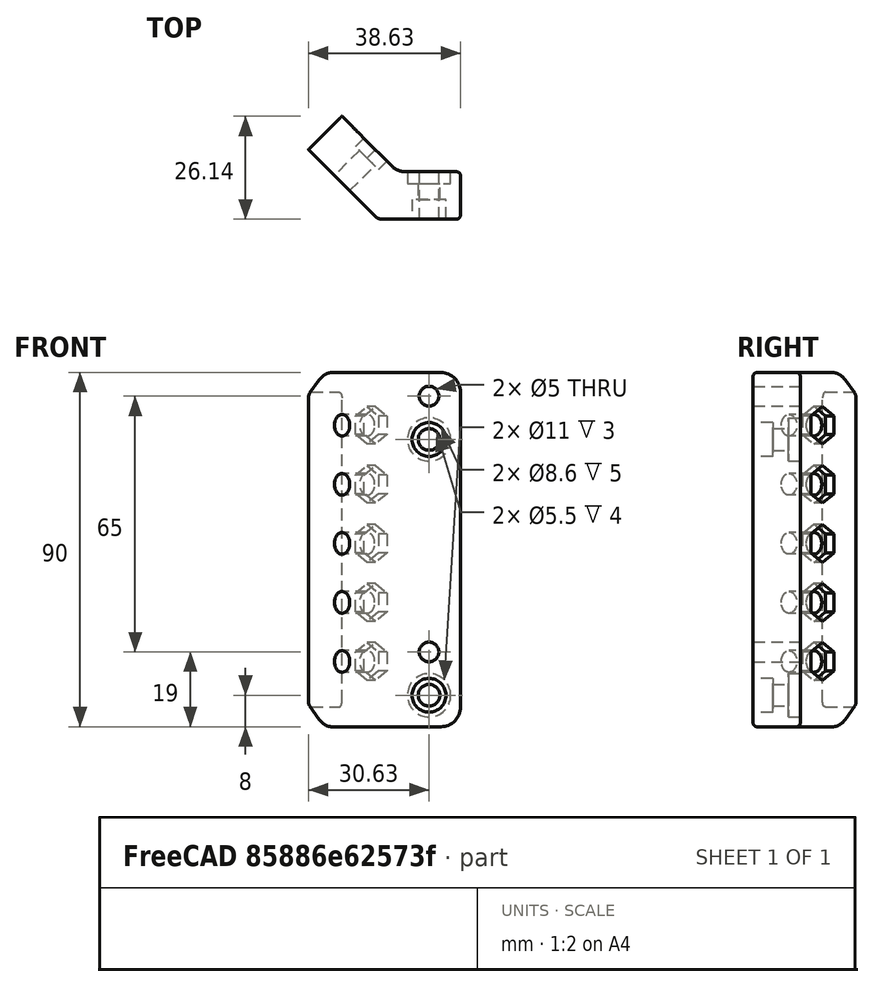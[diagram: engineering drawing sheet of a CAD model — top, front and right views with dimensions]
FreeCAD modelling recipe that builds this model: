
FCSTD DOCUMENT  (FreeCAD 0.19R)
Label: CargiFork
License: All rights reserved
LicenseURL: http://en.wikipedia.org/wiki/All_rights_reserved
objects: Sketcher::SketchObject×7, PartDesign::Pocket×6, PartDesign::Fillet×6, PartDesign::Pad×1, PartDesign::Chamfer×1, PartDesign::Body×1, Mesh::Feature×1
note: 36 computed .brp shape members not serialized (recipe doc carries the construction recipe); baked Part::Feature solids carry a one-line shape summary decoded from their .brp

FEATURE [Sketcher::SketchObject] Sketch
  FullyConstrained = true
  MapMode = 5
  Support = -> [XY_Plane]
  sketch-geometry (6):
    g0: LineSegment StartX=-16 StartY=0 StartZ=0 EndX=0 EndY=0 EndZ=0
    g1: LineSegment StartX=0 StartY=0 StartZ=0 EndX=0 EndY=-12 EndZ=0
    g2: LineSegment StartX=0 StartY=-12 StartZ=0 EndX=-20.9706 EndY=-12 EndZ=0
    g3: LineSegment StartX=-20.9706 StartY=-12 StartZ=0 EndX=-38.6274 EndY=5.65685 EndZ=0
    g4: LineSegment StartX=-38.6274 StartY=5.65685 StartZ=0 EndX=-30.1421 EndY=14.1421 EndZ=0
    g5: LineSegment StartX=-30.1421 StartY=14.1421 StartZ=0 EndX=-16 EndY=0 EndZ=0
  constraints (17):
    c: PointOnObject(g0,g-1)
    c: Coincident(g0,g-1)
    c: Coincident(g0,g1)
    c: PointOnObject(g1,g-2)
    c: Coincident(g1,g2)
    c: Horizontal(g2)
    c: Coincident(g2,g3)
    c: Coincident(g3,g4)
    c: Coincident(g4,g5)
    c: Coincident(g5,g0)
    c: Distance(g1) = 12
    c: Distance(g4) = 12
    c: Perpendicular(g3,g4)
    c: Angle(g5) = -0.785398
    c: Parallel(g3,g5)
    c: Distance(g0) = 16
    c: Distance(g5) = 20
FEATURE [PartDesign::Pad] Pad
  Direction = (1,1,1)
  Length = 90
  Length2 = 100
  Profile = -> Sketch
  Type = 0
FEATURE [Sketcher::SketchObject] Sketch001
  FullyConstrained = true
  MapMode = 5
  Placement = pos=(0,0,0) rot=(0,0.707107,0.707107;3.14159rad)
  Support = -> [Pad]
  sketch-geometry (2):
    g0: Circle CenterX=8 CenterY=73 CenterZ=0 NormalX=0 NormalY=0 NormalZ=1 AngleXU=0 Radius=2.75
    g1: Circle CenterX=8 CenterY=8 CenterZ=0 NormalX=0 NormalY=0 NormalZ=1 AngleXU=0 Radius=2.75
  constraints (6):
    c: Radius(g1) = 2.75
    c: Equal(g1,g0)
    c: DistanceY(g1) = 8
    c: Distance(g1,g0) = 65
    c: DistanceX(g-1,g0) = 8
    c: DistanceX(g1) = 8
FEATURE [PartDesign::Pocket] Pocket
  BaseFeature = -> Pad
  Length = 5
  Length2 = 100
  Profile = -> Sketch001
  Type = 1
FEATURE [Sketcher::SketchObject] Sketch002
  ExternalGeometry = -> [Pocket]
  FullyConstrained = true
  MapMode = 5
  Placement = pos=(0,0,0) rot=(0,0.707107,0.707107;3.14159rad)
  Support = -> [Pocket]
  sketch-geometry (2):
    g0: Circle CenterX=8 CenterY=73 CenterZ=0 NormalX=0 NormalY=0 NormalZ=1 AngleXU=0 Radius=5.5
    g1: Circle CenterX=8 CenterY=8 CenterZ=0 NormalX=0 NormalY=0 NormalZ=1 AngleXU=0 Radius=5.5
  constraints (4):
    c: Radius(g1) = 5.5
    c: Equal(g1,g0)
    c: Coincident(g1,g-4)
    c: Coincident(g0,g-3)
FEATURE [PartDesign::Pocket] Pocket001
  BaseFeature = -> Pocket
  Length = 3
  Length2 = 100
  Profile = -> Sketch002
  Type = 0
FEATURE [Sketcher::SketchObject] Sketch003
  ExternalGeometry = -> [Pocket001]
  FullyConstrained = true
  MapMode = 5
  Placement = pos=(0,-12,0) rot=(1,0,0;1.5708rad)
  Support = -> [Pocket001]
  sketch-geometry (2):
    g0: Circle CenterX=-8 CenterY=73 CenterZ=0 NormalX=0 NormalY=0 NormalZ=1 AngleXU=0 Radius=4.3
    g1: Circle CenterX=-8 CenterY=8 CenterZ=0 NormalX=0 NormalY=0 NormalZ=1 AngleXU=0 Radius=4.3
  constraints (4):
    c: Radius(g1) = 4.3
    c: Equal(g1,g0)
    c: Coincident(g1,g-4)
    c: Coincident(g0,g-3)
FEATURE [PartDesign::Pocket] Pocket002
  BaseFeature = -> Pocket001
  Length = 5
  Length2 = 100
  Profile = -> Sketch003
  Type = 0
FEATURE [Sketcher::SketchObject] Sketch004
  FullyConstrained = false
  MapMode = 5
  Placement = pos=(-16.4853,-16.4853,0) rot=(0.862856,-0.357407,-0.357407;1.71777rad)
  Support = -> [Pocket002]
  sketch-geometry (6):
    g0: Circle CenterX=-19.2578 CenterY=76.595 CenterZ=0 NormalX=0 NormalY=0 NormalZ=1 AngleXU=0 Radius=2.75
    g1: Circle CenterX=-19.2578 CenterY=61.595 CenterZ=0 NormalX=0 NormalY=0 NormalZ=1 AngleXU=0 Radius=2.75
    g2: Circle CenterX=-19.2578 CenterY=46.595 CenterZ=0 NormalX=0 NormalY=0 NormalZ=1 AngleXU=0 Radius=2.75
    g3: Circle CenterX=-19.2578 CenterY=31.595 CenterZ=0 NormalX=0 NormalY=0 NormalZ=1 AngleXU=0 Radius=2.75
    g4: Circle CenterX=-19.2578 CenterY=16.595 CenterZ=0 NormalX=0 NormalY=0 NormalZ=1 AngleXU=0 Radius=2.75
    g5: LineSegment StartX=-19.2578 StartY=117.649 StartZ=0 EndX=-19.2578 EndY=-34.6142 EndZ=0
  constraints (15):
    c: Radius(g0) = 2.75
    c: Equal(g0,g1)
    c: Equal(g0,g2)
    c: Equal(g0,g3)
    c: Vertical(g5)
    c: PointOnObject(g1,g5)
    c: PointOnObject(g0,g5)
    c: PointOnObject(g2,g5)
    c: PointOnObject(g3,g5)
    c: PointOnObject(g4,g5)
    c: Distance(g0,g1) = 15
    c: Distance(g2,g1) = 15
    c: Distance(g3,g2) = 15
    c: Distance(g4,g3) = 15
    c: Radius(g4) = 2.75
FEATURE [PartDesign::Pocket] Pocket003
  BaseFeature = -> Pocket002
  Length = 5
  Length2 = 100
  Profile = -> Sketch004
  Type = 1
FEATURE [Sketcher::SketchObject] Sketch005
  ExternalGeometry = -> [Pocket003]
  FullyConstrained = true
  MapMode = 5
  Placement = pos=(-8,-8,0) rot=(0.281085,0.678598,0.678598;2.59356rad)
  Support = -> [Pocket003]
  sketch-geometry (35):
    g0: LineSegment StartX=19.2578 StartY=71.803 StartZ=0 EndX=23.4078 EndY=74.199 EndZ=0
    g1: LineSegment StartX=23.4078 StartY=74.199 StartZ=0 EndX=23.4078 EndY=78.991 EndZ=0
    g2: LineSegment StartX=23.4078 StartY=78.991 StartZ=0 EndX=19.2578 EndY=81.387 EndZ=0
    g3: LineSegment StartX=19.2578 StartY=81.387 StartZ=0 EndX=15.1078 EndY=78.991 EndZ=0
    g4: LineSegment StartX=15.1078 StartY=78.991 StartZ=0 EndX=15.1078 EndY=74.199 EndZ=0
    g5: LineSegment StartX=15.1078 StartY=74.199 StartZ=0 EndX=19.2578 EndY=71.803 EndZ=0
    g6: Circle CenterX=19.2578 CenterY=76.595 CenterZ=0 NormalX=0 NormalY=0 NormalZ=1 AngleXU=0 Radius=4.79201
    g7: LineSegment StartX=23.4078 StartY=59.199 StartZ=0 EndX=23.4078 EndY=63.991 EndZ=0
    g8: LineSegment StartX=23.4078 StartY=63.991 StartZ=0 EndX=19.2578 EndY=66.387 EndZ=0
    g9: LineSegment StartX=19.2578 StartY=66.387 StartZ=0 EndX=15.1078 EndY=63.991 EndZ=0
    g10: LineSegment StartX=15.1078 StartY=63.991 StartZ=0 EndX=15.1078 EndY=59.199 EndZ=0
    g11: LineSegment StartX=15.1078 StartY=59.199 StartZ=0 EndX=19.2578 EndY=56.803 EndZ=0
    g12: LineSegment StartX=19.2578 StartY=56.803 StartZ=0 EndX=23.4078 EndY=59.199 EndZ=0
    g13: Circle CenterX=19.2578 CenterY=61.595 CenterZ=0 NormalX=0 NormalY=0 NormalZ=1 AngleXU=0 Radius=4.79201
    g14: LineSegment StartX=19.2578 StartY=41.803 StartZ=0 EndX=23.4078 EndY=44.199 EndZ=0
    g15: LineSegment StartX=23.4078 StartY=44.199 StartZ=0 EndX=23.4078 EndY=48.991 EndZ=0
    g16: LineSegment StartX=23.4078 StartY=48.991 StartZ=0 EndX=19.2578 EndY=51.387 EndZ=0
    g17: LineSegment StartX=19.2578 StartY=51.387 StartZ=0 EndX=15.1078 EndY=48.991 EndZ=0
    g18: LineSegment StartX=15.1078 StartY=48.991 StartZ=0 EndX=15.1078 EndY=44.199 EndZ=0
    g19: LineSegment StartX=15.1078 StartY=44.199 StartZ=0 EndX=19.2578 EndY=41.803 EndZ=0
    g20: Circle CenterX=19.2578 CenterY=46.595 CenterZ=0 NormalX=0 NormalY=0 NormalZ=1 AngleXU=0 Radius=4.79201
    g21: LineSegment StartX=19.2578 StartY=26.803 StartZ=0 EndX=23.4078 EndY=29.199 EndZ=0
    g22: LineSegment StartX=23.4078 StartY=29.199 StartZ=0 EndX=23.4078 EndY=33.991 EndZ=0
    g23: LineSegment StartX=23.4078 StartY=33.991 StartZ=0 EndX=19.2578 EndY=36.387 EndZ=0
    g24: LineSegment StartX=19.2578 StartY=36.387 StartZ=0 EndX=15.1078 EndY=33.991 EndZ=0
    g25: LineSegment StartX=15.1078 StartY=33.991 StartZ=0 EndX=15.1078 EndY=29.199 EndZ=0
    g26: LineSegment StartX=15.1078 StartY=29.199 StartZ=0 EndX=19.2578 EndY=26.803 EndZ=0
    g27: Circle CenterX=19.2578 CenterY=31.595 CenterZ=0 NormalX=0 NormalY=0 NormalZ=1 AngleXU=0 Radius=4.79201
    g28: LineSegment StartX=19.2578 StartY=11.803 StartZ=0 EndX=23.4078 EndY=14.199 EndZ=0
    g29: LineSegment StartX=23.4078 StartY=14.199 StartZ=0 EndX=23.4078 EndY=18.991 EndZ=0
    g30: LineSegment StartX=23.4078 StartY=18.991 StartZ=0 EndX=19.2578 EndY=21.387 EndZ=0
    g31: LineSegment StartX=19.2578 StartY=21.387 StartZ=0 EndX=15.1078 EndY=18.991 EndZ=0
    g32: LineSegment StartX=15.1078 StartY=18.991 StartZ=0 EndX=15.1078 EndY=14.199 EndZ=0
    g33: LineSegment StartX=15.1078 StartY=14.199 StartZ=0 EndX=19.2578 EndY=11.803 EndZ=0
    g34: Circle CenterX=19.2578 CenterY=16.595 CenterZ=0 NormalX=0 NormalY=0 NormalZ=1 AngleXU=0 Radius=4.79201
  constraints (80):
    c: Coincident(g0,g1)
    c: Coincident(g1,g2)
    c: Coincident(g2,g3)
    c: Coincident(g3,g4)
    c: Coincident(g4,g5)
    c: Coincident(g5,g0)
    c: Equal(g0, g1-g5) x5
    c: PointOnObject(g0,g6)
    c: PointOnObject(g1,g6)
    c: PointOnObject(g2,g6)
    c: PointOnObject(g3,g6)
    c: PointOnObject(g4,g6)
    c: PointOnObject(g5,g6)
    c: Distance(g0,g1) = 8.3
    c: Coincident(g6,g-3)
    c: Coincident(g7,g8)
    c: Coincident(g8,g9)
    c: Coincident(g9,g10)
    c: Coincident(g10,g11)
    c: Coincident(g11,g12)
    c: Coincident(g12,g7)
    c: Equal(g7, g8-g12) x5
    c: PointOnObject(g7,g13)
    c: PointOnObject(g8,g13)
    c: PointOnObject(g9,g13)
    c: PointOnObject(g10,g13)
    c: PointOnObject(g11,g13)
    c: PointOnObject(g12,g13)
    c: Coincident(g14,g15)
    c: Coincident(g15,g16)
    c: Coincident(g16,g17)
    c: Coincident(g17,g18)
    c: Coincident(g18,g19)
    c: Coincident(g19,g14)
    c: Equal(g14, g15-g19) x5
    c: PointOnObject(g14,g20)
    c: PointOnObject(g15,g20)
    c: PointOnObject(g16,g20)
    c: PointOnObject(g17,g20)
    c: PointOnObject(g18,g20)
    c: PointOnObject(g19,g20)
    c: Coincident(g21,g22)
    c: Coincident(g22,g23)
    c: Coincident(g23,g24)
    c: Coincident(g24,g25)
    c: Coincident(g25,g26)
    c: Coincident(g26,g21)
    c: Equal(g21, g22-g26) x5
    c: PointOnObject(g21,g27)
    c: PointOnObject(g22,g27)
    c: PointOnObject(g23,g27)
    c: PointOnObject(g24,g27)
    c: PointOnObject(g25,g27)
    c: PointOnObject(g26,g27)
    c: Coincident(g28,g29)
    c: Coincident(g29,g30)
    c: Coincident(g30,g31)
    c: Coincident(g31,g32)
    c: Coincident(g32,g33)
    c: Coincident(g33,g28)
    c: Equal(g28, g29-g33) x5
    c: PointOnObject(g28,g34)
    c: PointOnObject(g29,g34)
    c: PointOnObject(g30,g34)
    c: PointOnObject(g31,g34)
    c: PointOnObject(g32,g34)
    c: PointOnObject(g33,g34)
    c: Distance(g28,g30) = 8.3
    c: Distance(g21,g23) = 8.3
    c: Distance(g14,g16) = 8.3
    c: Distance(g7,g8) = 8.3
    c: Coincident(g34,g-7)
    c: Coincident(g27,g-6)
    c: Coincident(g20,g-5)
    c: Coincident(g13,g-4)
    c: Vertical(g1)
    c: Vertical(g7)
    c: Vertical(g15)
    c: Vertical(g22)
    c: Vertical(g29)
FEATURE [PartDesign::Pocket] Pocket004
  BaseFeature = -> Pocket003
  Length = 3
  Length2 = 100
  Profile = -> Sketch005
  Type = 0
FEATURE [Sketcher::SketchObject] Sketch006
  FullyConstrained = true
  MapMode = 5
  Placement = pos=(0,0,0) rot=(0,0.707107,0.707107;3.14159rad)
  Support = -> [Pocket004]
  sketch-geometry (2):
    g0: Circle CenterX=8 CenterY=84 CenterZ=0 NormalX=0 NormalY=0 NormalZ=1 AngleXU=0 Radius=2.5
    g1: Circle CenterX=8 CenterY=19 CenterZ=0 NormalX=0 NormalY=0 NormalZ=1 AngleXU=0 Radius=2.5
  constraints (6):
    c: Radius(g1) = 2.5
    c: Equal(g1,g0)
    c: DistanceX(g0) = 8
    c: DistanceX(g1) = 8
    c: Distance(g0,g1) = 65
    c: DistanceY(g1) = 19
FEATURE [PartDesign::Pocket] Pocket005
  BaseFeature = -> Pocket004
  Length = 5
  Length2 = 100
  Profile = -> Sketch006
  Type = 1
FEATURE [PartDesign::Fillet] Fillet
  Base = -> Pocket005 [Edge46,Edge42]
  BaseFeature = -> Pocket005
  Radius = 5
  SupportTransform = false
FEATURE [PartDesign::Chamfer] Chamfer
  Angle = 45
  Base = -> Fillet [Edge14,Edge54]
  BaseFeature = -> Fillet
  ChamferType = 0
  FlipDirection = false
  Size = 5
  Size2 = 1
  SupportTransform = false
FEATURE [PartDesign::Fillet] Fillet001
  Base = -> Chamfer [Edge2,Edge71]
  BaseFeature = -> Chamfer
  Radius = 6
  SupportTransform = false
FEATURE [PartDesign::Fillet] Fillet002
  Base = -> Fillet001 [Edge54]
  BaseFeature = -> Fillet001
  Radius = 2
  SupportTransform = false
FEATURE [PartDesign::Fillet] Fillet003
  Base = -> Fillet002 [Edge35]
  BaseFeature = -> Fillet002
  Radius = 5
  SupportTransform = false
FEATURE [PartDesign::Fillet] Fillet004
  Base = -> Fillet003 [Edge5]
  BaseFeature = -> Fillet003
  Radius = 1
  SupportTransform = false
FEATURE [PartDesign::Fillet] Fillet005
  Base = -> Fillet004 [Edge3]
  BaseFeature = -> Fillet004
  Radius = 1
  SupportTransform = false
FEATURE [PartDesign::Body] Body
  Group = -> [Sketch,Pad,Sketch001,Pocket,Sketch002,Pocket001,Sketch003,Pocket002,Sketch004,Pocket003,Sketch005,Pocket004,Sketch006,Pocket005,Fillet,Chamfer,Fillet001,Fillet002,Fillet003,Fillet004,Fillet005]
  Origin = -> Origin
  Tip = -> Fillet005
FEATURE [Mesh::Feature] Mesh  label="Fillet005 (Meshed)"
